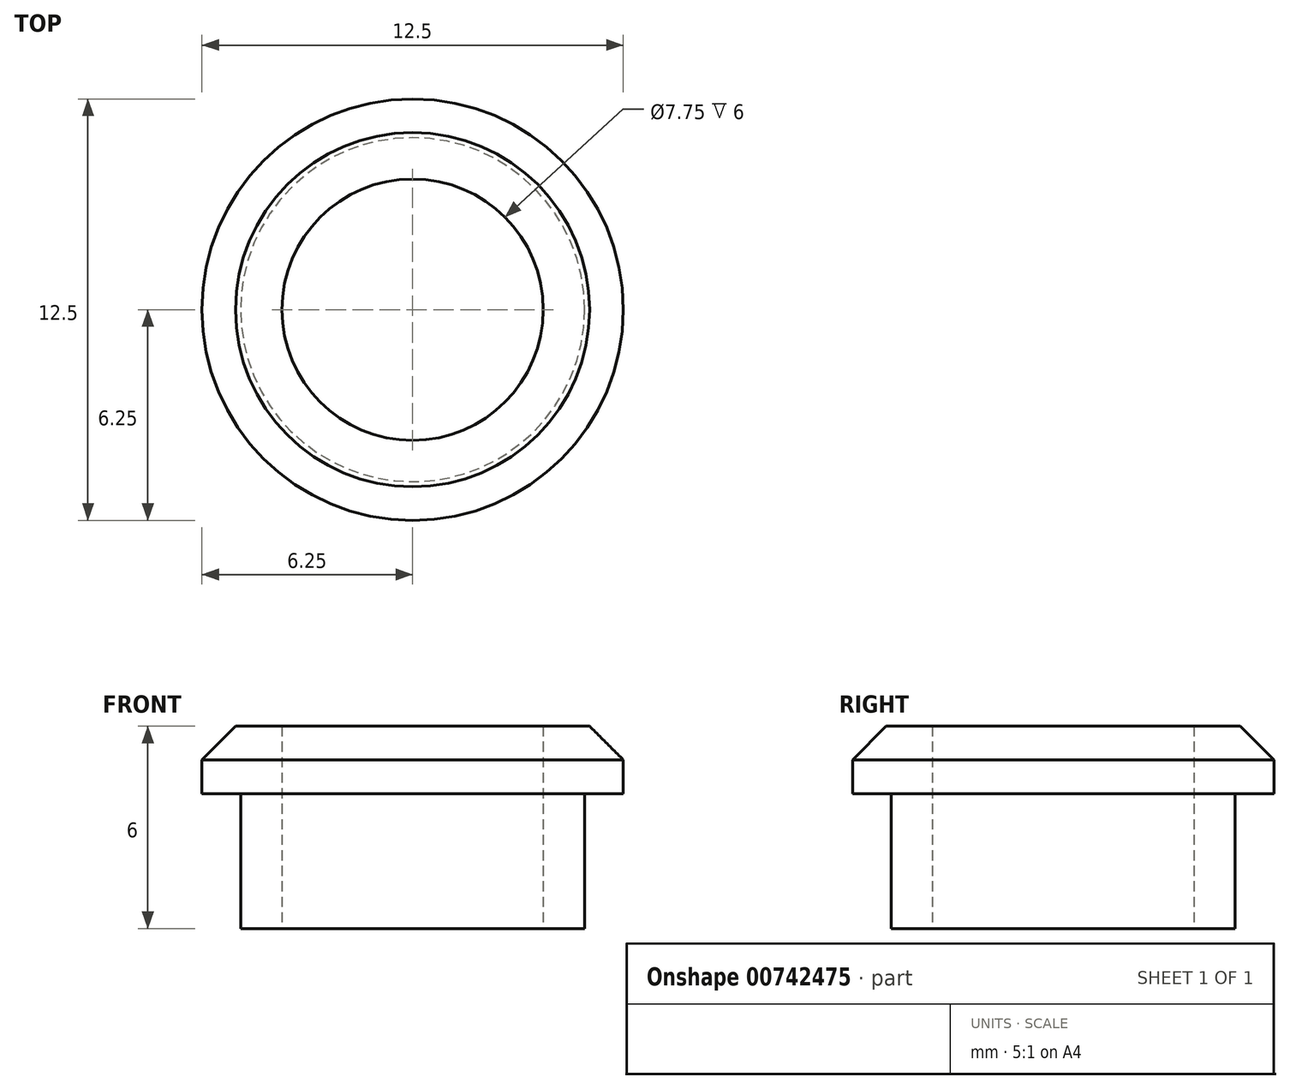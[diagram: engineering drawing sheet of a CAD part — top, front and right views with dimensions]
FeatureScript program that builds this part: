
annotation { "Feature Type Name" : "Feature", "Feature Type Description" : "" }
export const myFeature = defineFeature(function(context is Context, id is Id, definition is map)
    precondition{}
    {
        {
            var Q0;
            Q0=qCreatedBy(makeId("Top.planeOp"),FACE);
            var sketch = newSketch(context, id + "F0", { "sketchPlane" : qUnion([Q0])});
            skCircle(sketch, "E0", {"center": v(0, 0) * mm, "radius": 5.1 * mm});
            skCircle(sketch, "E1", {"center": v(0, 0) * mm, "radius": 3.88 * mm});
            skCircle(sketch, "E2", {"center": v(0, 0) * mm, "radius": 6.25 * mm});
            skSolve(sketch);
        }
        {
            var Q0;
            Q0=makeQuery(id+"F0.imprint","IMPRINT",FACE,{"disambiguationData":[TD([[makeQuery(id+"F0.imprint","IMPRINT",EDGE,{"derivedFrom":sQuery(id+"F0.wireOp",EDGE,"E0")}),1.0]])]});
            extrude(context, id + "F1", {"entities" : qUnion([Q0]), "depth" : 6 * mm, "offsetDistance" : 25 * mm});
        }
        {
            var Q0;
            Q0 = qSketchRegion(id + "F0", true);
            extrude(context, id + "F2", {"entities" : qUnion([Q0]), "operationType" : NewBodyOperationType.ADD, "depth" : 6 * mm, "offsetDistance" : 25 * mm, "hasSecondDirection" : true, "secondDirectionOppositeDirection" : false, "secondDirectionDepth" : 4 * mm});
        }
        {
            var Q0;
            Q0=makeQuery(id+"F2.opExtrude","CAP_EDGE",EDGE,{"disambiguationData":[OSD([sQuery(id+"F0.wireOp",EDGE,"E2")])],"isStart":false});
            chamfer(context, id + "F3", {"entities" : qUnion([Q0]), "width" : 1 * mm, "tangentPropagation" : true});
        }
    });
